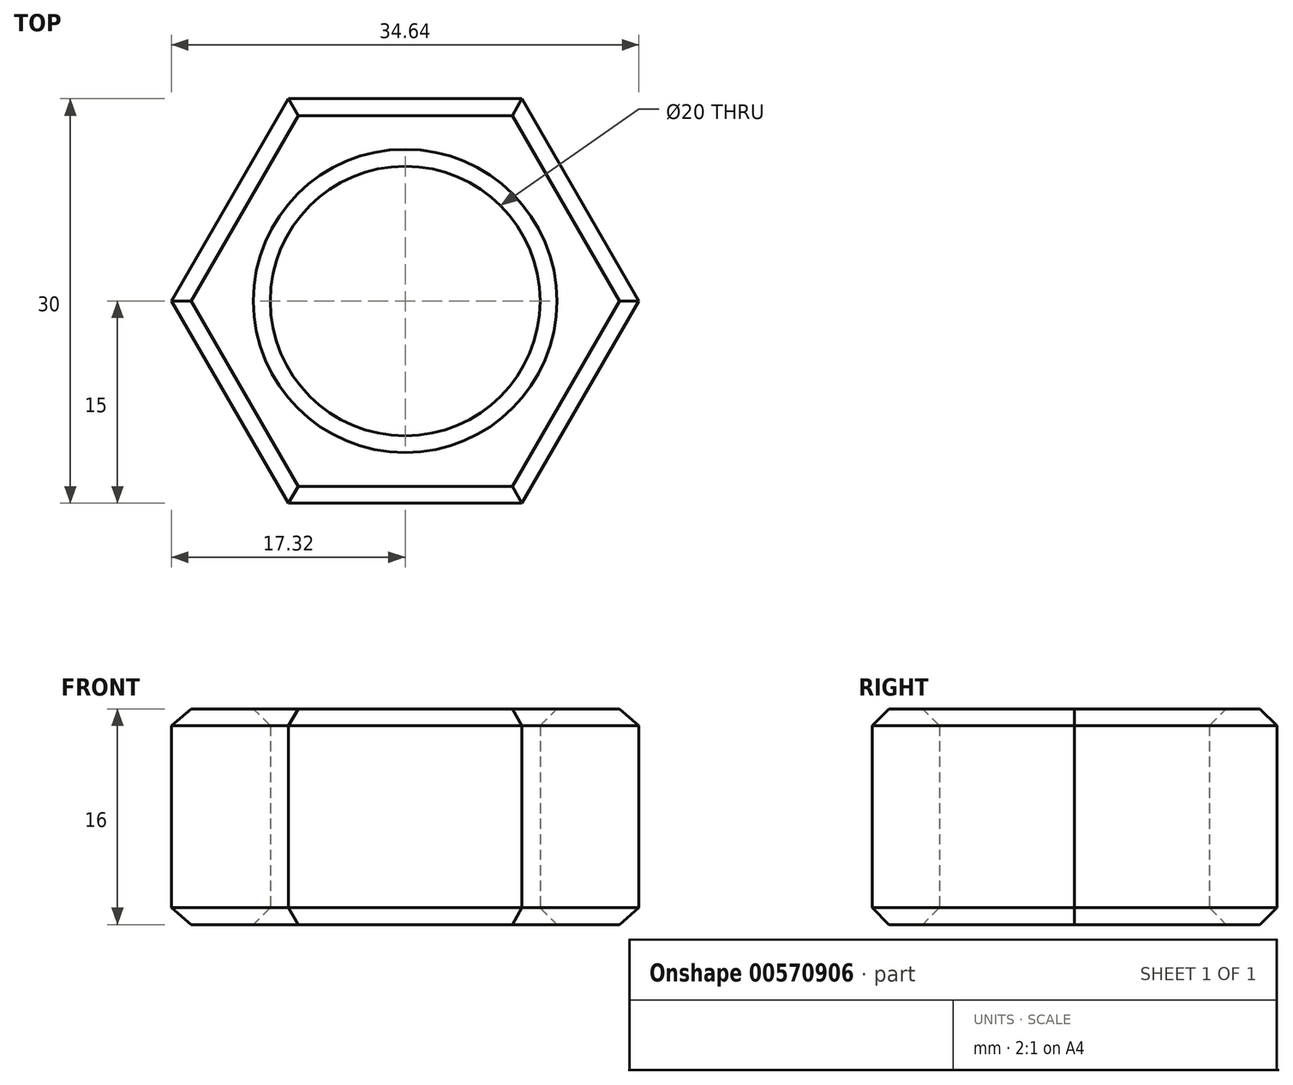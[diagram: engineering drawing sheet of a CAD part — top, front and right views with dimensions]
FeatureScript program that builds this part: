
annotation { "Feature Type Name" : "Feature", "Feature Type Description" : "" }
export const myFeature = defineFeature(function(context is Context, id is Id, definition is map)
    precondition{}
    {
        {
            var Q0;
            Q0=qCreatedBy(makeId("Top.planeOp"),FACE);
            var sketch = newSketch(context, id + "F0", { "sketchPlane" : qUnion([Q0])});
            skCircle(sketch, "E0", {"center": v(0, 0) * mm, "radius": 10 * mm});
            skCircle(sketch, "E1.cCircle", {"center": v(0, 0) * mm, "radius": 15 * mm, "construction": true});
            skLineSegment(sketch, "E1.0", {"start": v(17.32, 0) * mm, "end": v(8.66, -15) * mm});
            skLineSegment(sketch, "E1.1", {"start": v(8.66, -15) * mm, "end": v(-8.66, -15) * mm});
            skLineSegment(sketch, "E1.2", {"start": v(-8.66, -15) * mm, "end": v(-17.32, 0) * mm});
            skLineSegment(sketch, "E1.3", {"start": v(-17.32, 0) * mm, "end": v(-8.66, 15) * mm});
            skLineSegment(sketch, "E1.4", {"start": v(-8.66, 15) * mm, "end": v(8.66, 15) * mm});
            skLineSegment(sketch, "E1.5", {"start": v(8.66, 15) * mm, "end": v(17.32, 0) * mm});
            skPoint(sketch, "E1.0.midPoint", {"position": v(13, -7.5) * mm});
            skSolve(sketch);
        }
        {
            var Q0;
            Q0=makeQuery(id+"F0.imprint","IMPRINT",FACE,{"disambiguationData":[TD([[makeQuery(id+"F0.imprint","IMPRINT",EDGE,{"derivedFrom":sQuery(id+"F0.wireOp",EDGE,"E0")}),-1.0]])]});
            extrude(context, id + "F1", {"entities" : qUnion([Q0]), "depth" : 16 * mm, "offsetDistance" : 25 * mm});
        }
        {
            var Q0;
            Q0=makeQuery(id+"F1.opExtrude","CAP_FACE",FACE,{"disambiguationData":[OSD([sQuery(id+"F0.wireOp",EDGE,"E0"),sQuery(id+"F0.wireOp",EDGE,"E1.0"),sQuery(id+"F0.wireOp",EDGE,"E1.1"),sQuery(id+"F0.wireOp",EDGE,"E1.2"),sQuery(id+"F0.wireOp",EDGE,"E1.3"),sQuery(id+"F0.wireOp",EDGE,"E1.4"),sQuery(id+"F0.wireOp",EDGE,"E1.5")])],"isStart":false});
            var Q1;
            Q1=makeQuery(id+"F1.opExtrude","CAP_FACE",FACE,{"disambiguationData":[OSD([sQuery(id+"F0.wireOp",EDGE,"E0"),sQuery(id+"F0.wireOp",EDGE,"E1.0"),sQuery(id+"F0.wireOp",EDGE,"E1.1"),sQuery(id+"F0.wireOp",EDGE,"E1.2"),sQuery(id+"F0.wireOp",EDGE,"E1.3"),sQuery(id+"F0.wireOp",EDGE,"E1.4"),sQuery(id+"F0.wireOp",EDGE,"E1.5")])],"isStart":true});
            chamfer(context, id + "F2", {"entities" : qUnion([Q0, Q1]), "width" : 1.25 * mm, "tangentPropagation" : true});
        }
    });
